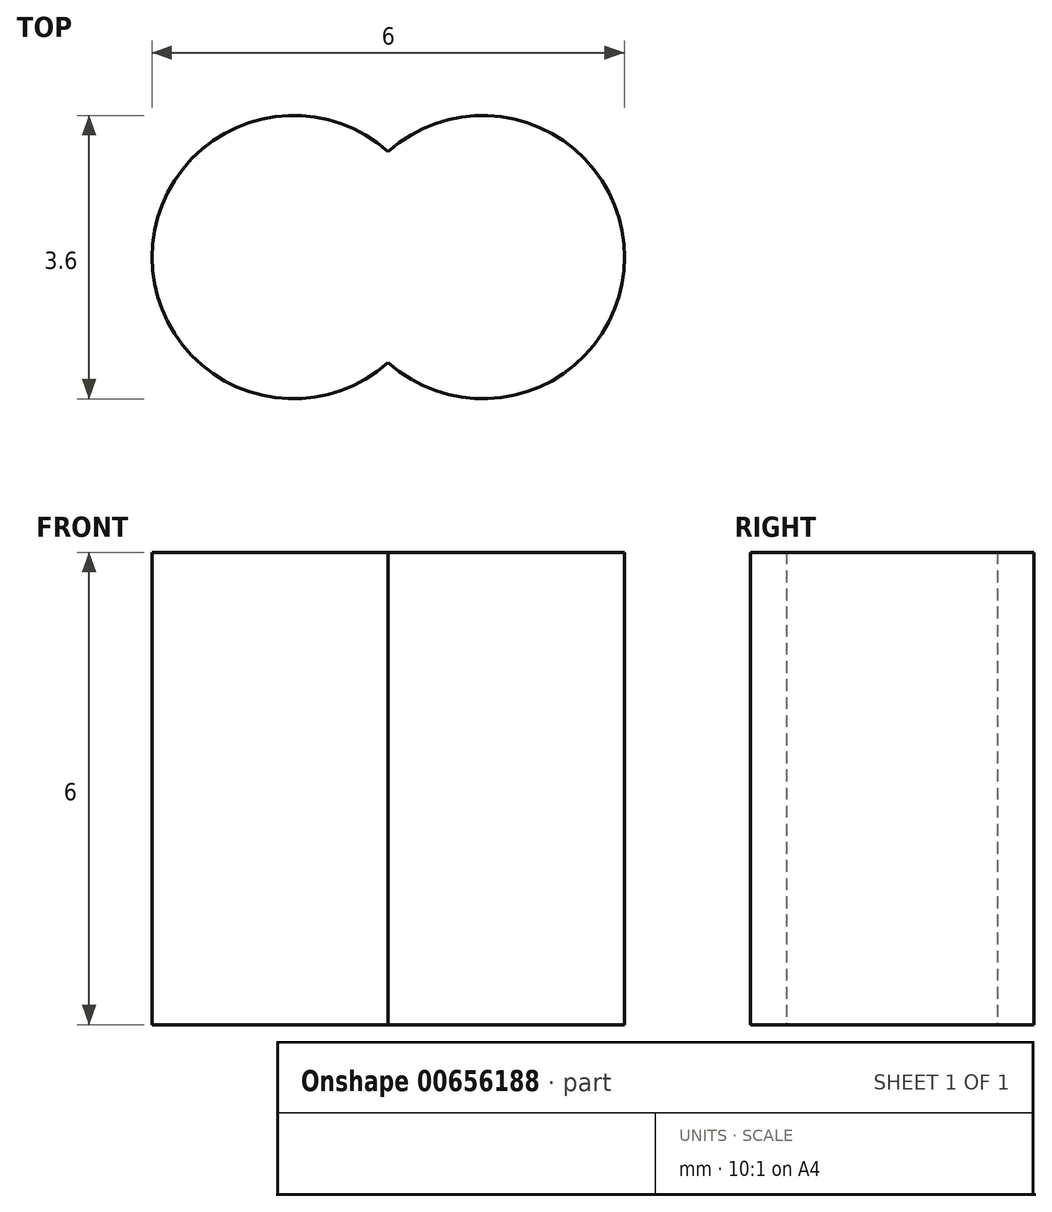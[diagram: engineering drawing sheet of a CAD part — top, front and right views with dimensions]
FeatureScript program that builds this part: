
annotation { "Feature Type Name" : "Feature", "Feature Type Description" : "" }
export const myFeature = defineFeature(function(context is Context, id is Id, definition is map)
    precondition{}
    {
        {
            var Q0;
            Q0=qCreatedBy(makeId("Top.planeOp"),FACE);
            var sketch = newSketch(context, id + "F0", { "sketchPlane" : qUnion([Q0])});
            skCircle(sketch, "E0", {"center": v(-2.4, 0) * mm, "radius": 1.8 * mm});
            skCircle(sketch, "E1", {"center": v(0, 0) * mm, "radius": 1.8 * mm});
            skSolve(sketch);
        }
        {
            var Q0;
            {var subQ0=sQuery(id+"F0.wireOp",EDGE,"E1");var subQ1=sQuery(id+"F0.wireOp",EDGE,"E0");var subQ2=makeQuery(id+"F0.imprint","INTERSECT",VERTEX,{"disambiguationData":[OD(0.0)],"derivedFrom":[subQ1,subQ0]});Q0=makeQuery(id+"F0.imprint","IMPRINT",FACE,{"disambiguationData":[TD([[makeQuery(id+"F0.imprint","IMPRINT",EDGE,{"disambiguationData":[TD([[subQ2,1.0]])],"derivedFrom":subQ1}),1.0]])]});}
            var Q1;
            {var subQ0=sQuery(id+"F0.wireOp",EDGE,"E1");var subQ1=sQuery(id+"F0.wireOp",EDGE,"E0");var subQ2=makeQuery(id+"F0.imprint","INTERSECT",VERTEX,{"disambiguationData":[OD(0.0)],"derivedFrom":[subQ1,subQ0]});Q1=makeQuery(id+"F0.imprint","IMPRINT",FACE,{"disambiguationData":[TD([[makeQuery(id+"F0.imprint","IMPRINT",EDGE,{"disambiguationData":[TD([[subQ2,-1.0]])],"derivedFrom":subQ1}),1.0]])]});}
            var Q2;
            {var subQ0=sQuery(id+"F0.wireOp",EDGE,"E1");var subQ1=sQuery(id+"F0.wireOp",EDGE,"E0");var subQ2=makeQuery(id+"F0.imprint","INTERSECT",VERTEX,{"disambiguationData":[OD(0.0)],"derivedFrom":[subQ1,subQ0]});Q2=makeQuery(id+"F0.imprint","IMPRINT",FACE,{"disambiguationData":[TD([[makeQuery(id+"F0.imprint","IMPRINT",EDGE,{"disambiguationData":[TD([[subQ2,-1.0]])],"derivedFrom":subQ1}),-1.0]])]});}
            extrude(context, id + "F1", {"entities" : qUnion([Q0, Q1, Q2]), "depth" : 6 * mm, "offsetDistance" : 25 * mm});
        }
    });
